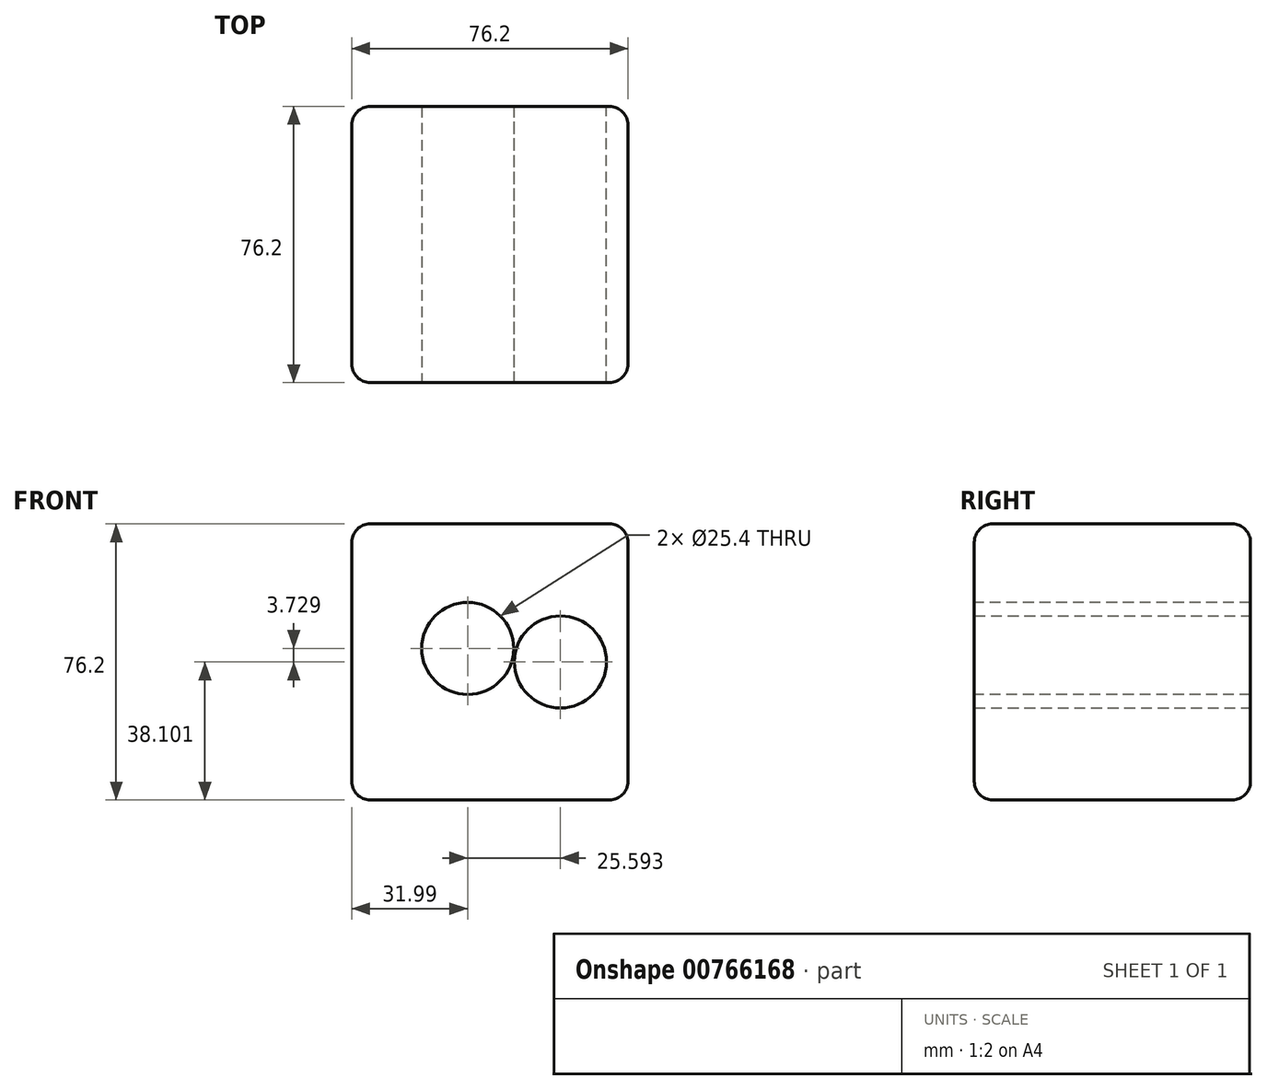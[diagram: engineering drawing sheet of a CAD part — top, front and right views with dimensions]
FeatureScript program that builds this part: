
annotation { "Feature Type Name" : "Feature", "Feature Type Description" : "" }
export const myFeature = defineFeature(function(context is Context, id is Id, definition is map)
    precondition{}
    {
        {
            var Q0;
            Q0=qCreatedBy(makeId("Front.planeOp"),FACE);
            var sketch = newSketch(context, id + "F0", { "sketchPlane" : qUnion([Q0])});
            skLineSegment(sketch, "E0.bottom", {"start": v(-31.99, 34.37) * mm, "end": v(44.21, 34.37) * mm});
            skLineSegment(sketch, "E0.top", {"start": v(-31.99, -41.83) * mm, "end": v(44.21, -41.83) * mm});
            skLineSegment(sketch, "E0.left", {"start": v(-31.99, 34.37) * mm, "end": v(-31.99, -41.83) * mm});
            skLineSegment(sketch, "E0.right", {"start": v(44.21, 34.37) * mm, "end": v(44.21, -41.83) * mm});
            skSolve(sketch);
        }
        {
            var Q0;
            Q0 = qSketchRegion(id + "F0", true);
            extrude(context, id + "F1", {"entities" : qUnion([Q0]), "depth" : 76.2 * mm, "offsetDistance" : 25.4 * mm});
        }
        {
            var Q0;
            Q0=makeQuery(id+"F1.opExtrude","SWEPT_EDGE",EDGE,{"disambiguationData":[OSD([sQuery(id+"F0.wireOp",EDGE,"E0.bottom"),sQuery(id+"F0.wireOp",EDGE,"E0.right")])]});
            var Q1;
            Q1=makeQuery(id+"F1.opExtrude","CAP_EDGE",EDGE,{"disambiguationData":[OSD([sQuery(id+"F0.wireOp",EDGE,"E0.bottom")])],"isStart":false});
            var Q2;
            Q2=makeQuery(id+"F1.opExtrude","CAP_EDGE",EDGE,{"disambiguationData":[OSD([sQuery(id+"F0.wireOp",EDGE,"E0.right")])],"isStart":false});
            var Q3;
            Q3=makeQuery(id+"F1.opExtrude","SWEPT_EDGE",EDGE,{"disambiguationData":[OSD([sQuery(id+"F0.wireOp",EDGE,"E0.top"),sQuery(id+"F0.wireOp",EDGE,"E0.right")])]});
            var Q4;
            Q4=makeQuery(id+"F1.opExtrude","CAP_EDGE",EDGE,{"disambiguationData":[OSD([sQuery(id+"F0.wireOp",EDGE,"E0.top")])],"isStart":false});
            var Q5;
            Q5=makeQuery(id+"F1.opExtrude","SWEPT_EDGE",EDGE,{"disambiguationData":[OSD([sQuery(id+"F0.wireOp",EDGE,"E0.bottom"),sQuery(id+"F0.wireOp",EDGE,"E0.left")])]});
            var Q6;
            Q6=makeQuery(id+"F1.opExtrude","CAP_EDGE",EDGE,{"disambiguationData":[OSD([sQuery(id+"F0.wireOp",EDGE,"E0.bottom")])],"isStart":true});
            var Q7;
            Q7=makeQuery(id+"F1.opExtrude","CAP_EDGE",EDGE,{"disambiguationData":[OSD([sQuery(id+"F0.wireOp",EDGE,"E0.right")])],"isStart":true});
            var Q8;
            Q8=makeQuery(id+"F1.opExtrude","CAP_EDGE",EDGE,{"disambiguationData":[OSD([sQuery(id+"F0.wireOp",EDGE,"E0.top")])],"isStart":true});
            var Q9;
            Q9=makeQuery(id+"F1.opExtrude","SWEPT_EDGE",EDGE,{"disambiguationData":[OSD([sQuery(id+"F0.wireOp",EDGE,"E0.top"),sQuery(id+"F0.wireOp",EDGE,"E0.left")])]});
            var Q10;
            Q10=makeQuery(id+"F1.opExtrude","CAP_EDGE",EDGE,{"disambiguationData":[OSD([sQuery(id+"F0.wireOp",EDGE,"E0.left")])],"isStart":true});
            var Q11;
            Q11=makeQuery(id+"F1.opExtrude","CAP_EDGE",EDGE,{"disambiguationData":[OSD([sQuery(id+"F0.wireOp",EDGE,"E0.left")])],"isStart":false});
            fillet(context, id + "F2", {"entities" : qUnion([Q0, Q1, Q2, Q3, Q4, Q5, Q6, Q7, Q8, Q9, Q10, Q11]), "radius" : 5.08 * mm, "tangentPropagation" : true, "allowEdgeOverflow" : false});
        }
        {
            var Q0;
            Q0=makeQuery(id+"F1.opExtrude","CAP_FACE",FACE,{"disambiguationData":[OSD([sQuery(id+"F0.wireOp",EDGE,"E0.bottom"),sQuery(id+"F0.wireOp",EDGE,"E0.top"),sQuery(id+"F0.wireOp",EDGE,"E0.left"),sQuery(id+"F0.wireOp",EDGE,"E0.right")])],"isStart":false});
            var sketch = newSketch(context, id + "F3", { "sketchPlane" : qUnion([Q0])});
            skCircle(sketch, "E1", {"center": v(0, 0) * mm, "radius": 12.7 * mm});
            skSolve(sketch);
        }
        {
            var Q0;
            Q0=sQuery(id+"F3.wireOp",VERTEX,"E1.center");
            var Q1;
            Q1=makeQuery(id+"F1.opExtrude","SWEPT_BODY",BODY,{"disambiguationData":[OSD([sQuery(id+"F0.wireOp",EDGE,"E0.bottom"),sQuery(id+"F0.wireOp",EDGE,"E0.top"),sQuery(id+"F0.wireOp",EDGE,"E0.left"),sQuery(id+"F0.wireOp",EDGE,"E0.right")])]});
            hole(context, id + "F4", {"style" : HoleStyle.SIMPLE, "endStyle" : HoleEndStyle.THROUGH, "holeDiameter" : 25.4 * mm, "majorDiameter" : 6.35 * mm, "isTappedThrough" : true, "tappedDepth" : 12.7 * mm, "tapClearance" : 3, "locations" : qUnion([Q0]), "scope" : qUnion([Q1])});
        }
        {
            var Q0;
            Q0=makeQuery(id+"F1.opExtrude","CAP_FACE",FACE,{"disambiguationData":[OSD([sQuery(id+"F0.wireOp",EDGE,"E0.bottom"),sQuery(id+"F0.wireOp",EDGE,"E0.top"),sQuery(id+"F0.wireOp",EDGE,"E0.left"),sQuery(id+"F0.wireOp",EDGE,"E0.right")])],"isStart":true});
            var sketch = newSketch(context, id + "F5", { "sketchPlane" : qUnion([Q0])});
            skCircle(sketch, "E2", {"center": v(-25.6, -3.73) * mm, "radius": 12.7 * mm});
            skSolve(sketch);
        }
        {
            var Q0;
            Q0=sQuery(id+"F5.wireOp",VERTEX,"E2.center");
            var Q1;
            Q1=makeQuery(id+"F1.opExtrude","SWEPT_BODY",BODY,{"disambiguationData":[OSD([sQuery(id+"F0.wireOp",EDGE,"E0.bottom"),sQuery(id+"F0.wireOp",EDGE,"E0.top"),sQuery(id+"F0.wireOp",EDGE,"E0.left"),sQuery(id+"F0.wireOp",EDGE,"E0.right")])]});
            hole(context, id + "F6", {"style" : HoleStyle.SIMPLE, "endStyle" : HoleEndStyle.THROUGH, "holeDiameter" : 25.4 * mm, "majorDiameter" : 6.35 * mm, "isTappedThrough" : true, "tappedDepth" : 12.7 * mm, "tapClearance" : 3, "locations" : qUnion([Q0]), "scope" : qUnion([Q1])});
        }
    });
